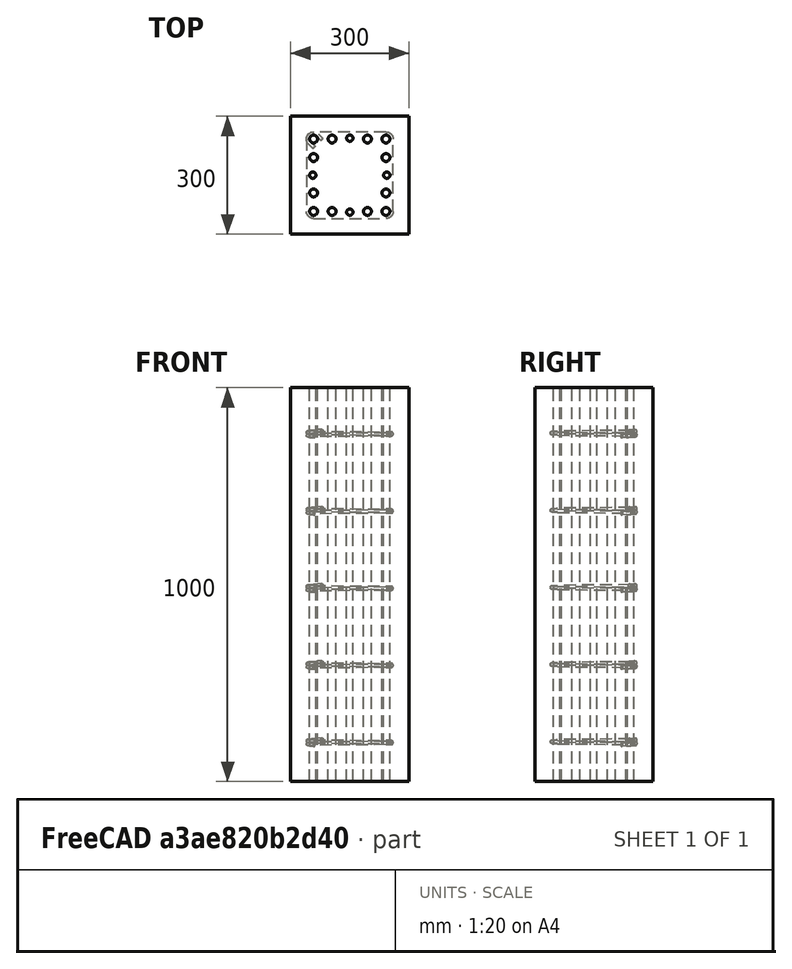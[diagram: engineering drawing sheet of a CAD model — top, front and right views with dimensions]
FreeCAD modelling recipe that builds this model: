
FCSTD DOCUMENT  (FreeCAD 0.21R33771 (Git))
Label: column
License: All rights reserved
LicenseURL: https://en.wikipedia.org/wiki/All_rights_reserved
objects: Part::FeaturePython×16, Sketcher::SketchObject×14, App::DocumentObjectGroupPython×6, Part::Part2DObjectPython×2
note: 32 computed .brp shape members not serialized (recipe doc carries the construction recipe); baked Part::Feature solids carry a one-line shape summary decoded from their .brp

FEATURE [Part::Part2DObjectPython] Rectangle  # Draft 2D object (typed FeaturePython)
  Area = 90000
  ChamferSize = 0
  Columns = 1
  FilletRadius = 0
  Height = 300
  Length = 300
  MakeFace = true
  Rows = 1
FEATURE [Part::FeaturePython] Structure  # Arch/BIM 13 (typed FeaturePython)
  Base = -> Rectangle
  BaseMirror = false
  BaseOffsetX = 0
  BaseOffsetY = 0
  BasePerpendicularToTool = false
  BaseRotation = 0
  ComputedLength = 1000
  FaceMaker = 0
  Height = 1000
  HorizontalArea = 90000
  IfcData = attributes={"GlobalId": {"name": "GlobalId", "type": "IfcGloballyUniqueId", "is_enum": false, "enum_values": []}, "Description": {"... (+484 chars omitted),+1 more (map truncated)
  IfcType = 13
  Length = 0
  MoveBase = false
  MoveWithHost = false
  Nodes = (2) [(150,150,0),(150,150,1000)]
  NodesOffset = 0
  Normal = (0,0,0)
  PerimeterLength = 1200
  PredefinedType = 0
  ToolOffsetFirst = 0
  ToolOffsetLast = 0
  VerticalArea = 1200000
  Width = 100
FEATURE [Sketcher::SketchObject] Sketch
  FullyConstrained = false
  MapMode = 5
  Placement = pos=(0,300,0) rot=(0,0.707107,0.707107;3.14159rad)
  Support = -> [Structure]
  sketch-geometry (1):
    g0: LineSegment StartX=-58 StartY=0 StartZ=0 EndX=-58 EndY=1000 EndZ=0
FEATURE [Part::FeaturePython] Rebar  label="StraightRebar"  # Arch/BIM 110 (typed FeaturePython)
  Amount = 2
  AmountCheck = true
  Base = -> Sketch
  Cover = 48
  CoverAlong = Right Side
  Diameter = 20
  Direction = (0,0,0)
  Distance = 0
  FrontCover = 48
  HorizontalArea = 0
  Host = -> Structure
  IfcType = 110
  LeftBottomCover = 0
  Length = 1000
  Mark = StraightRebar
  MoveBase = false
  MoveWithHost = false
  OffsetEnd = 58
  OffsetStart = 58
  Orientation = Vertical
  PerimeterLength = 0
  PlacementList = 2 placements: [(0,-58,1.28786e-14),(0,-242,5.37348e-14)]
  RebarShape = 0
  RightTopCover = 0
  Rounding = 0
  Spacing = 184
  TotalLength = 2000
  TrueSpacing = 2
  VerticalArea = 0
FEATURE [Sketcher::SketchObject] Sketch001
  FullyConstrained = false
  MapMode = 5
  Placement = pos=(0,300,0) rot=(0,0.707107,0.707107;3.14159rad)
  Support = -> [Structure]
  sketch-geometry (1):
    g0: LineSegment StartX=-242 StartY=0 StartZ=0 EndX=-242 EndY=1000 EndZ=0
FEATURE [Part::FeaturePython] Rebar001  label="StraightRebar001"  # Arch/BIM 110 (typed FeaturePython)
  Amount = 2
  AmountCheck = true
  Base = -> Sketch001
  Cover = 48
  CoverAlong = Left Side
  Diameter = 20
  Direction = (0,0,0)
  Distance = 0
  FrontCover = 48
  HorizontalArea = 0
  Host = -> Structure
  IfcType = 110
  LeftBottomCover = 0
  Length = 1000
  Mark = StraightRebar001
  MoveBase = false
  MoveWithHost = false
  OffsetEnd = 58
  OffsetStart = 58
  Orientation = Vertical
  PerimeterLength = 0
  PlacementList = 2 placements: [(0,-58,1.28786e-14),(0,-242,5.37348e-14)]
  RebarShape = 0
  RightTopCover = 0
  Rounding = 0
  Spacing = 184
  TotalLength = 2000
  TrueSpacing = 2
  VerticalArea = 0
FEATURE [Part::Part2DObjectPython] Wire  # Draft 2D object (typed FeaturePython)
  Area = 0
  ChamferSize = 0
  Closed = false
  End = (59.4142,220.787,-10.9339)
  FilletRadius = 0
  Length = 987.335
  MakeFace = true
  Points = (7) [(79.2132,240.586,2.18678),(44,275.799,0),(44,44,-2.18678),(256,44,-4.37357),(256,256,-6.56035),(24.201,256,-8.74713),(59.4142,220.787,-10.9339)]
  Start = (79.2132,240.586,2.18678)
  Subdivisions = 0
  Support = -> [Structure]
FEATURE [Part::FeaturePython] Rebar002  label="Stirrup"  # Arch/BIM 110 (typed FeaturePython)
  Amount = 5
  AmountCheck = true
  Base = -> Wire
  BentAngle = 135
  BentFactor = 2
  BottomCover = 40
  Diameter = 8
  Direction = (0,0,1)
  Distance = 0
  FrontCover = 100
  HorizontalArea = 0
  Host = -> Structure
  IfcType = 110
  LeftCover = 40
  Length = 987.335
  Mark = Stirrup
  MoveBase = false
  MoveWithHost = false
  OffsetEnd = 104
  OffsetStart = 104
  PerimeterLength = 0
  PlacementList = 5 placements: arithmetic series from (0,0,104) step (0,0,196) to (0,0,888)
  RebarShape = 3
  RightCover = 40
  Rounding = 1.75
  Spacing = 196
  TopCover = 40
  TotalLength = 4936.68
  TrueSpacing = 5
  VerticalArea = 0
FEATURE [App::DocumentObjectGroupPython] Ties  # scripted group (container) (typed FeaturePython)
  BottomCover = 40
  Group = -> [Rebar002]
  LeftCover = 40
  RightCover = 40
  Ties = -> [Rebar002]
  TiesConfiguration = SingleTie
  TopCover = 40
FEATURE [App::DocumentObjectGroupPython] MainRebars  # scripted group (container) (typed FeaturePython)
  BottomOffset = 0
  Group = -> [Rebar,Rebar001]
  HookExtendAlong = x-axis
  HookExtension = 40
  HookOrientation = Top Inside
  MainRebars = -> [Rebar,Rebar001]
  RebarType = StraightRebar
  TopOffset = 0
FEATURE [Sketcher::SketchObject] Sketch002
  FullyConstrained = false
  MapMode = 5
  Placement = pos=(0,0,0) rot=(0.57735,-0.57735,-0.57735;2.0944rad)
  Support = -> [Structure]
  sketch-geometry (1):
    g0: LineSegment StartX=-58 StartY=0 StartZ=0 EndX=-58 EndY=1000 EndZ=0
FEATURE [Part::FeaturePython] Rebar003  label="StraightRebar002"  # Arch/BIM 110 (typed FeaturePython)
  Amount = 1
  AmountCheck = true
  Base = -> Sketch002
  Cover = 48
  CoverAlong = Right Side
  Diameter = 20
  Direction = (0,0,0)
  Distance = 0
  FrontCover = 95
  HorizontalArea = 0
  Host = -> Structure
  IfcType = 110
  LeftBottomCover = 0
  Length = 1000
  Mark = StraightRebar002
  MoveBase = false
  MoveWithHost = false
  OffsetEnd = 195
  OffsetStart = 105
  Orientation = Vertical
  PerimeterLength = 0
  PlacementList = 1 placements: [(105,0,0)]
  RebarShape = 0
  RightTopCover = 0
  Rounding = 0
  Spacing = 0
  TotalLength = 1000
  TrueSpacing = 1
  VerticalArea = 0
FEATURE [Sketcher::SketchObject] Sketch003
  FullyConstrained = false
  MapMode = 5
  Placement = pos=(0,0,0) rot=(0.57735,-0.57735,-0.57735;2.0944rad)
  Support = -> [Structure]
  sketch-geometry (1):
    g0: LineSegment StartX=-56 StartY=0 StartZ=0 EndX=-56 EndY=1000 EndZ=0
FEATURE [Part::FeaturePython] Rebar004  label="StraightRebar003"  # Arch/BIM 110 (typed FeaturePython)
  Amount = 1
  AmountCheck = true
  Base = -> Sketch003
  Cover = 48
  CoverAlong = Right Side
  Diameter = 16
  Direction = (0,0,0)
  Distance = 0
  FrontCover = 142
  HorizontalArea = 0
  Host = -> Structure
  IfcType = 110
  LeftBottomCover = 0
  Length = 1000
  Mark = StraightRebar003
  MoveBase = false
  MoveWithHost = false
  OffsetEnd = 150
  OffsetStart = 150
  Orientation = Vertical
  PerimeterLength = 0
  PlacementList = 1 placements: [(150,0,0)]
  RebarShape = 0
  RightTopCover = 0
  Rounding = 0
  Spacing = 0
  TotalLength = 1000
  TrueSpacing = 1
  VerticalArea = 0
FEATURE [Sketcher::SketchObject] Sketch004
  FullyConstrained = false
  MapMode = 5
  Placement = pos=(0,0,0) rot=(0.57735,-0.57735,-0.57735;2.0944rad)
  Support = -> [Structure]
  sketch-geometry (1):
    g0: LineSegment StartX=-58 StartY=0 StartZ=0 EndX=-58 EndY=1000 EndZ=0
FEATURE [Part::FeaturePython] Rebar005  label="StraightRebar004"  # Arch/BIM 110 (typed FeaturePython)
  Amount = 1
  AmountCheck = true
  Base = -> Sketch004
  Cover = 48
  CoverAlong = Right Side
  Diameter = 20
  Direction = (0,0,0)
  Distance = 0
  FrontCover = 185
  HorizontalArea = 0
  Host = -> Structure
  IfcType = 110
  LeftBottomCover = 0
  Length = 1000
  Mark = StraightRebar004
  MoveBase = false
  MoveWithHost = false
  OffsetEnd = 105
  OffsetStart = 195
  Orientation = Vertical
  PerimeterLength = 0
  PlacementList = 1 placements: [(195,0,0)]
  RebarShape = 0
  RightTopCover = 0
  Rounding = 0
  Spacing = 0
  TotalLength = 1000
  TrueSpacing = 1
  VerticalArea = 0
FEATURE [Sketcher::SketchObject] Sketch005
  FullyConstrained = false
  MapMode = 5
  Placement = pos=(0,0,0) rot=(0.57735,-0.57735,-0.57735;2.0944rad)
  Support = -> [Structure]
  sketch-geometry (1):
    g0: LineSegment StartX=-242 StartY=0 StartZ=0 EndX=-242 EndY=1000 EndZ=0
FEATURE [Part::FeaturePython] Rebar006  label="StraightRebar005"  # Arch/BIM 110 (typed FeaturePython)
  Amount = 1
  AmountCheck = true
  Base = -> Sketch005
  Cover = 48
  CoverAlong = Left Side
  Diameter = 20
  Direction = (0,0,0)
  Distance = 0
  FrontCover = 95
  HorizontalArea = 0
  Host = -> Structure
  IfcType = 110
  LeftBottomCover = 0
  Length = 1000
  Mark = StraightRebar005
  MoveBase = false
  MoveWithHost = false
  OffsetEnd = 195
  OffsetStart = 105
  Orientation = Vertical
  PerimeterLength = 0
  PlacementList = 1 placements: [(105,0,0)]
  RebarShape = 0
  RightTopCover = 0
  Rounding = 0
  Spacing = 0
  TotalLength = 1000
  TrueSpacing = 1
  VerticalArea = 0
FEATURE [Sketcher::SketchObject] Sketch006
  FullyConstrained = false
  MapMode = 5
  Placement = pos=(0,0,0) rot=(0.57735,-0.57735,-0.57735;2.0944rad)
  Support = -> [Structure]
  sketch-geometry (1):
    g0: LineSegment StartX=-244 StartY=0 StartZ=0 EndX=-244 EndY=1000 EndZ=0
FEATURE [Part::FeaturePython] Rebar007  label="StraightRebar006"  # Arch/BIM 110 (typed FeaturePython)
  Amount = 1
  AmountCheck = true
  Base = -> Sketch006
  Cover = 48
  CoverAlong = Left Side
  Diameter = 16
  Direction = (0,0,0)
  Distance = 0
  FrontCover = 142
  HorizontalArea = 0
  Host = -> Structure
  IfcType = 110
  LeftBottomCover = 0
  Length = 1000
  Mark = StraightRebar006
  MoveBase = false
  MoveWithHost = false
  OffsetEnd = 150
  OffsetStart = 150
  Orientation = Vertical
  PerimeterLength = 0
  PlacementList = 1 placements: [(150,0,0)]
  RebarShape = 0
  RightTopCover = 0
  Rounding = 0
  Spacing = 0
  TotalLength = 1000
  TrueSpacing = 1
  VerticalArea = 0
FEATURE [Sketcher::SketchObject] Sketch007
  FullyConstrained = false
  MapMode = 5
  Placement = pos=(0,0,0) rot=(0.57735,-0.57735,-0.57735;2.0944rad)
  Support = -> [Structure]
  sketch-geometry (1):
    g0: LineSegment StartX=-242 StartY=0 StartZ=0 EndX=-242 EndY=1000 EndZ=0
FEATURE [Part::FeaturePython] Rebar008  label="StraightRebar007"  # Arch/BIM 110 (typed FeaturePython)
  Amount = 1
  AmountCheck = true
  Base = -> Sketch007
  Cover = 48
  CoverAlong = Left Side
  Diameter = 20
  Direction = (0,0,0)
  Distance = 0
  FrontCover = 185
  HorizontalArea = 0
  Host = -> Structure
  IfcType = 110
  LeftBottomCover = 0
  Length = 1000
  Mark = StraightRebar007
  MoveBase = false
  MoveWithHost = false
  OffsetEnd = 105
  OffsetStart = 195
  Orientation = Vertical
  PerimeterLength = 0
  PlacementList = 1 placements: [(195,0,0)]
  RebarShape = 0
  RightTopCover = 0
  Rounding = 0
  Spacing = 0
  TotalLength = 1000
  TrueSpacing = 1
  VerticalArea = 0
FEATURE [Sketcher::SketchObject] Sketch008
  FullyConstrained = false
  MapMode = 5
  Placement = pos=(0,300,0) rot=(0,0.707107,0.707107;3.14159rad)
  Support = -> [Structure]
  sketch-geometry (1):
    g0: LineSegment StartX=-58 StartY=0 StartZ=0 EndX=-58 EndY=1000 EndZ=0
FEATURE [Part::FeaturePython] Rebar009  label="StraightRebar008"  # Arch/BIM 110 (typed FeaturePython)
  Amount = 1
  AmountCheck = true
  Base = -> Sketch008
  Cover = 48
  CoverAlong = Right Side
  Diameter = 20
  Direction = (0,0,0)
  Distance = 0
  FrontCover = 95
  HorizontalArea = 0
  Host = -> Structure
  IfcType = 110
  LeftBottomCover = 0
  Length = 1000
  Mark = StraightRebar008
  MoveBase = false
  MoveWithHost = false
  OffsetEnd = 195
  OffsetStart = 105
  Orientation = Vertical
  PerimeterLength = 0
  PlacementList = 1 placements: [(0,-105,2.33147e-14)]
  RebarShape = 0
  RightTopCover = 0
  Rounding = 0
  Spacing = 0
  TotalLength = 1000
  TrueSpacing = 1
  VerticalArea = 0
FEATURE [Sketcher::SketchObject] Sketch009
  FullyConstrained = false
  MapMode = 5
  Placement = pos=(0,300,0) rot=(0,0.707107,0.707107;3.14159rad)
  Support = -> [Structure]
  sketch-geometry (1):
    g0: LineSegment StartX=-56 StartY=0 StartZ=0 EndX=-56 EndY=1000 EndZ=0
FEATURE [Part::FeaturePython] Rebar010  label="StraightRebar009"  # Arch/BIM 110 (typed FeaturePython)
  Amount = 1
  AmountCheck = true
  Base = -> Sketch009
  Cover = 48
  CoverAlong = Right Side
  Diameter = 16
  Direction = (0,0,0)
  Distance = 0
  FrontCover = 142
  HorizontalArea = 0
  Host = -> Structure
  IfcType = 110
  LeftBottomCover = 0
  Length = 1000
  Mark = StraightRebar009
  MoveBase = false
  MoveWithHost = false
  OffsetEnd = 150
  OffsetStart = 150
  Orientation = Vertical
  PerimeterLength = 0
  PlacementList = 1 placements: [(0,-150,3.33067e-14)]
  RebarShape = 0
  RightTopCover = 0
  Rounding = 0
  Spacing = 0
  TotalLength = 1000
  TrueSpacing = 1
  VerticalArea = 0
FEATURE [Sketcher::SketchObject] Sketch010
  FullyConstrained = false
  MapMode = 5
  Placement = pos=(0,300,0) rot=(0,0.707107,0.707107;3.14159rad)
  Support = -> [Structure]
  sketch-geometry (1):
    g0: LineSegment StartX=-58 StartY=0 StartZ=0 EndX=-58 EndY=1000 EndZ=0
FEATURE [Part::FeaturePython] Rebar011  label="StraightRebar010"  # Arch/BIM 110 (typed FeaturePython)
  Amount = 1
  AmountCheck = true
  Base = -> Sketch010
  Cover = 48
  CoverAlong = Right Side
  Diameter = 20
  Direction = (0,0,0)
  Distance = 0
  FrontCover = 185
  HorizontalArea = 0
  Host = -> Structure
  IfcType = 110
  LeftBottomCover = 0
  Length = 1000
  Mark = StraightRebar010
  MoveBase = false
  MoveWithHost = false
  OffsetEnd = 105
  OffsetStart = 195
  Orientation = Vertical
  PerimeterLength = 0
  PlacementList = 1 placements: [(0,-195,4.32987e-14)]
  RebarShape = 0
  RightTopCover = 0
  Rounding = 0
  Spacing = 0
  TotalLength = 1000
  TrueSpacing = 1
  VerticalArea = 0
FEATURE [Sketcher::SketchObject] Sketch011
  FullyConstrained = false
  MapMode = 5
  Placement = pos=(0,300,0) rot=(0,0.707107,0.707107;3.14159rad)
  Support = -> [Structure]
  sketch-geometry (1):
    g0: LineSegment StartX=-242 StartY=0 StartZ=0 EndX=-242 EndY=1000 EndZ=0
FEATURE [Part::FeaturePython] Rebar012  label="StraightRebar011"  # Arch/BIM 110 (typed FeaturePython)
  Amount = 1
  AmountCheck = true
  Base = -> Sketch011
  Cover = 48
  CoverAlong = Left Side
  Diameter = 20
  Direction = (0,0,0)
  Distance = 0
  FrontCover = 95
  HorizontalArea = 0
  Host = -> Structure
  IfcType = 110
  LeftBottomCover = 0
  Length = 1000
  Mark = StraightRebar011
  MoveBase = false
  MoveWithHost = false
  OffsetEnd = 195
  OffsetStart = 105
  Orientation = Vertical
  PerimeterLength = 0
  PlacementList = 1 placements: [(0,-105,2.33147e-14)]
  RebarShape = 0
  RightTopCover = 0
  Rounding = 0
  Spacing = 0
  TotalLength = 1000
  TrueSpacing = 1
  VerticalArea = 0
FEATURE [Sketcher::SketchObject] Sketch012
  FullyConstrained = false
  MapMode = 5
  Placement = pos=(0,300,0) rot=(0,0.707107,0.707107;3.14159rad)
  Support = -> [Structure]
  sketch-geometry (1):
    g0: LineSegment StartX=-244 StartY=0 StartZ=0 EndX=-244 EndY=1000 EndZ=0
FEATURE [Part::FeaturePython] Rebar013  label="StraightRebar012"  # Arch/BIM 110 (typed FeaturePython)
  Amount = 1
  AmountCheck = true
  Base = -> Sketch012
  Cover = 48
  CoverAlong = Left Side
  Diameter = 16
  Direction = (0,0,0)
  Distance = 0
  FrontCover = 142
  HorizontalArea = 0
  Host = -> Structure
  IfcType = 110
  LeftBottomCover = 0
  Length = 1000
  Mark = StraightRebar012
  MoveBase = false
  MoveWithHost = false
  OffsetEnd = 150
  OffsetStart = 150
  Orientation = Vertical
  PerimeterLength = 0
  PlacementList = 1 placements: [(0,-150,3.33067e-14)]
  RebarShape = 0
  RightTopCover = 0
  Rounding = 0
  Spacing = 0
  TotalLength = 1000
  TrueSpacing = 1
  VerticalArea = 0
FEATURE [Sketcher::SketchObject] Sketch013
  FullyConstrained = false
  MapMode = 5
  Placement = pos=(0,300,0) rot=(0,0.707107,0.707107;3.14159rad)
  Support = -> [Structure]
  sketch-geometry (1):
    g0: LineSegment StartX=-242 StartY=0 StartZ=0 EndX=-242 EndY=1000 EndZ=0
FEATURE [Part::FeaturePython] Rebar014  label="StraightRebar013"  # Arch/BIM 110 (typed FeaturePython)
  Amount = 1
  AmountCheck = true
  Base = -> Sketch013
  Cover = 48
  CoverAlong = Left Side
  Diameter = 20
  Direction = (0,0,0)
  Distance = 0
  FrontCover = 185
  HorizontalArea = 0
  Host = -> Structure
  IfcType = 110
  LeftBottomCover = 0
  Length = 1000
  Mark = StraightRebar013
  MoveBase = false
  MoveWithHost = false
  OffsetEnd = 105
  OffsetStart = 195
  Orientation = Vertical
  PerimeterLength = 0
  PlacementList = 1 placements: [(0,-195,4.32987e-14)]
  RebarShape = 0
  RightTopCover = 0
  Rounding = 0
  Spacing = 0
  TotalLength = 1000
  TrueSpacing = 1
  VerticalArea = 0
FEATURE [App::DocumentObjectGroupPython] XDirRebars  # scripted group (container) (typed FeaturePython)
  BottomOffset = 0
  Group = -> [Rebar003,Rebar004,Rebar005,Rebar006,Rebar007,Rebar008]
  HookExtension = 0
  HookOrientation = Top Inside
  NumberDiameter = 1#20.0mm+1#16.0mm+1#20.0mm
  RebarType = StraightRebar
  TopOffset = 0
  XDirRebars = -> [Rebar003,Rebar004,Rebar005,Rebar006,Rebar007,Rebar008]
FEATURE [App::DocumentObjectGroupPython] YDirRebars  # scripted group (container) (typed FeaturePython)
  BottomOffset = 0
  Group = -> [Rebar009,Rebar010,Rebar011,Rebar012,Rebar013,Rebar014]
  HookExtension = 0
  HookOrientation = Top Inside
  NumberDiameter = 1#20mm+1#16mm+1#20mm
  RebarType = StraightRebar
  TopOffset = 0
  YDirRebars = -> [Rebar009,Rebar010,Rebar011,Rebar012,Rebar013,Rebar014]
FEATURE [App::DocumentObjectGroupPython] SecondaryRebars  # scripted group (container) (typed FeaturePython)
  Group = -> [XDirRebars,YDirRebars]
  SecondaryRebars = -> [XDirRebars,YDirRebars]
FEATURE [App::DocumentObjectGroupPython] ColumnReinforcement  # scripted group (container) (typed FeaturePython)
  ColumnType = RectangularColumn
  Group = -> [Ties,MainRebars,SecondaryRebars]
  RebarGroups = -> [Ties,MainRebars,SecondaryRebars]
